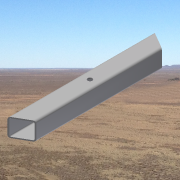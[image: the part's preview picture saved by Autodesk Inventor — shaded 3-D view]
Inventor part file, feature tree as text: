
AUTODESK INVENTOR PART (.ipt)
format: ipt  version: 2013 SP2 (Build 170200200, 200)  size: 168,448 bytes
history: native  units: in
note: dims shown in document units (in); Inventor stores cm internally (conversion verified against a paired STEP export)
features: sketch x3, extrude x2, hole x1
ambient origin geometry x8: Origin, YZ Plane, XZ Plane, XY Plane, X Axis, Y Axis, Z Axis, Center Point
bodies: Solid1 (feature_tree)
feature tree (6):
  extrude  "Extrusion1"  Depth=1.0in
  extrude  "Extrusion2"  Depth=0.065in
  hole  "Hole1"  [1 undecoded]
  sketch  "Sketch1"  dims[d0=1.0in d1=1.0in]
  sketch  "Sketch2"  dims[d2=0.125in d3=0.065in]
  sketch  "Sketch3"  dims[d4=8.0in d5=0.0in d10=8.0in d11=0.0in d12=0.25in d13=0.75in d14=0.375in d15=0.25in d16=0.5635in d17=1.0in d18=0.8108in]
note: 1 required parameter value undecoded (feature->parameter linkage not recoverable at this tier; creation-order binding heuristic only, values carry confidence <= 0.55)
